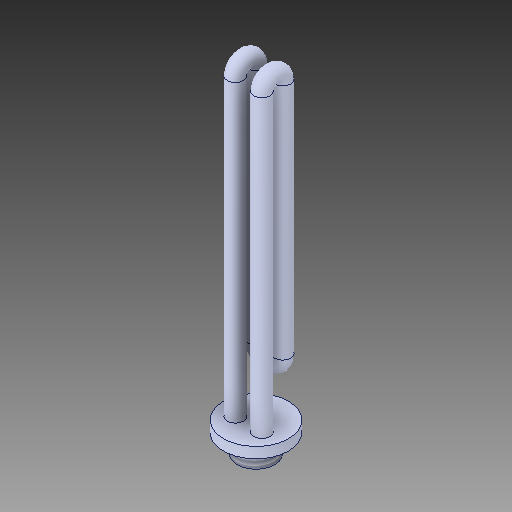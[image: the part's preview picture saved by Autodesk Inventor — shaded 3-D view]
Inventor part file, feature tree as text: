
AUTODESK INVENTOR PART (.ipt)
format: ipt  version: 2018 (Build 220112000, 112)  size: 158,208 bytes
history: native  units: in
note: dims shown in document units (in); Inventor stores cm internally (conversion verified against a paired STEP export)
features: extrude x1, chamfer x1, thread x1, sketch x1, projected_geometry x1, sweep x1
ambient origin geometry x8: Origin, YZ Plane, XZ Plane, XY Plane, X Axis, Y Axis, Z Axis, Center Point
bodies: Solid1 (feature_tree)
feature tree (6):
  extrude  "Extrusion1"  Depth=0.5in TaperAngle=0.0deg
  chamfer  "Chamfer1"  Distance=0.125in Angle=45.0deg
  thread  "Thread1"  [1 undecoded]
  sketch  "Sketch1"  dims[d0=1.0in d1=0.5in d2=0.0in d3=0.125in d4=0.0787in d5=45.0deg d6=0.3937in d7=0.0in]
  projected_geometry  "Projected Loop1"
  sweep  "Sweep4"
note: 1 required parameter value undecoded (feature->parameter linkage not recoverable at this tier; creation-order binding heuristic only, values carry confidence <= 0.55)
